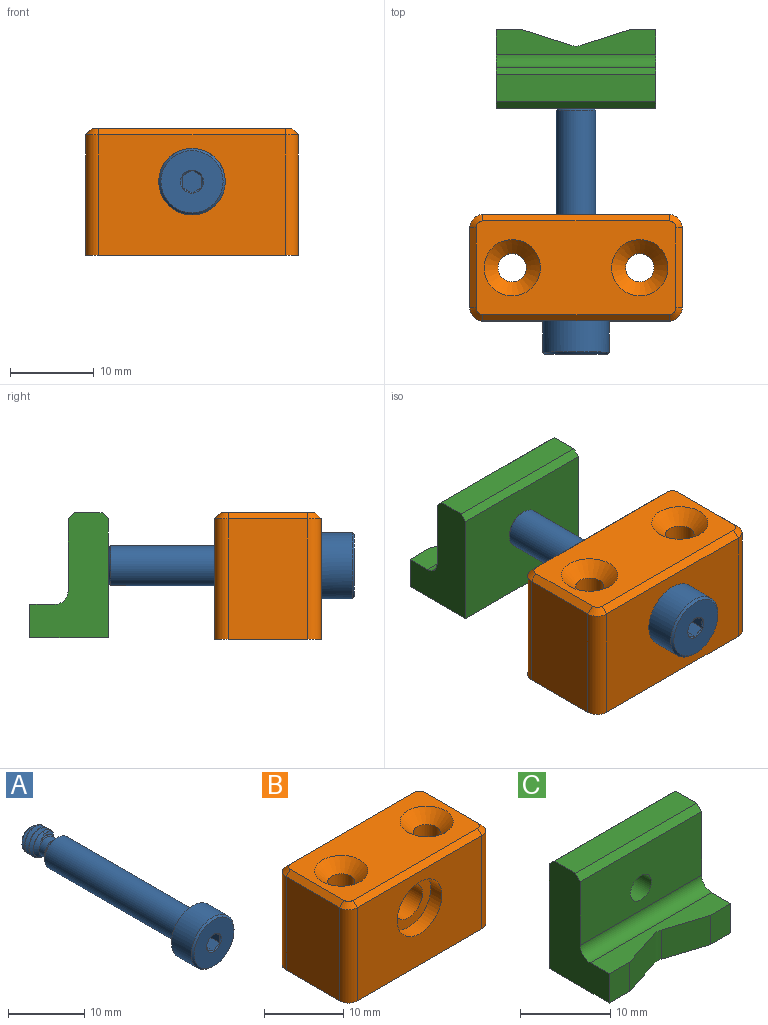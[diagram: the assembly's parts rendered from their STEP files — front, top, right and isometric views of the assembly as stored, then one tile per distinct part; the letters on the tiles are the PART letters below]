
ASSEMBLY  parts=3 mates=1
PART A: 31 faces, bbox 8.5x35x8.5 mm
  f0: cone r=1.42mm half-angle=45deg, axis (0,1,0), area 5.5mm2, adj f1,f6,f7,f8,f9
  f1: bspline ~4.17x4.17mm, area 20mm2, adj f0,f2,f4,f5,f6,f8
  f2: cone r=1.56mm half-angle=45deg, axis (0,-1,0), area 3.7mm2, adj f1,f3,f4,f7,f8
  f3: plane 3.12x3.12mm, normal (0,1,0), area 7.7mm2, adj f2
  f4: cone r=1.56mm half-angle=45deg, axis (0,-1,0), area 0.4mm2, adj f1,f2,f5,f7
  f5: cylinder r=2.08mm len=4.17mm, axis (0,1,0), area 3mm2, adj f1,f4,f6,f7
  f6: cone r=1.42mm half-angle=45deg, axis (0,1,0), area 0.4mm2, adj f0,f1,f5,f7
  f7: bspline ~4.17x4.17mm, area 20mm2, adj f0,f2,f4,f5,f6,f8
  f8: cylinder r=1.57mm len=3.13mm, axis (0,1,0), area 3.5mm2, adj f0,f1,f2,f7
  f9: cylinder r=1.42mm len=2.85mm, axis (0,1,0), area 9.8mm2, adj f0,f10
  f10: torus R=2.08mm, axis (0,1,0), area 10.8mm2, adj f9,f11
  f11: plane 4.25x4.25mm, normal (0,1,0), area 0.5mm2, adj f10,f12
  f12: cone r=2.12mm half-angle=45deg, axis (0,-1,0), area 5.2mm2, adj f11,f13
  f13: cylinder r=2.38mm len=25.14mm, axis (0,1,0), area 376.2mm2, adj f12,f14
  f14: plane 7.94x7.94mm, normal (0,1,0), area 31.7mm2, adj f13,f15
  f15: cylinder r=3.97mm len=7.94mm, axis (0,1,0), area 92.5mm2, adj f14,f16
  f16: cone r=3.97mm half-angle=45deg, axis (0,1,0), area 8.8mm2, adj f15,f17
  f17: plane 7.58x7.58mm, normal (0,-1,0), area 37.3mm2, adj f16,f18,f26,f27,f28,f29,f30
  f18: cone r=1.37mm half-angle=45deg, axis (0,-1,0), area 0mm2, adj f17,f19
  f19: plane 2.51x1.9mm, normal (-1,0,0), area 2.6mm2, adj f18,f20,f24,f25
  f20: plane 2.75x2.38mm, normal (0,-1,0), area 4.9mm2, adj f19,f21,f22,f23,f24,f25
  f21: plane 2.51x1.71mm, normal (0.5,0,0.87), area 2.6mm2, adj f20,f22,f25,f29
  f22: plane 2.51x1.9mm, normal (1,0,0), area 2.6mm2, adj f20,f21,f23,f28
  f23: plane 2.51x1.71mm, normal (0.5,0,-0.87), area 2.6mm2, adj f20,f22,f24,f27
  f24: plane 2.51x1.71mm, normal (-0.5,0,-0.87), area 2.6mm2, adj f19,f20,f23,f26
  f25: plane 2.51x1.71mm, normal (-0.5,0,0.87), area 2.6mm2, adj f19,f20,f21,f30
  f26: cone r=1.37mm half-angle=45deg, axis (0,-1,0), area 0mm2, adj f17,f24
  f27: cone r=1.37mm half-angle=45deg, axis (0,-1,0), area 0mm2, adj f17,f23
  f28: cone r=1.37mm half-angle=45deg, axis (0,-1,0), area 0mm2, adj f17,f22
  f29: cone r=1.37mm half-angle=45deg, axis (0,-1,0), area 0mm2, adj f17,f21
  f30: cone r=1.37mm half-angle=45deg, axis (0,-1,0), area 0mm2, adj f17,f25
PART B: 25 faces, bbox 25.4x12.7x15.2 mm
  f0: cylinder r=4mm len=8mm, axis (0,1,0), area 50.3mm2, adj f4,f24
  f1: plane 14.4x9.53mm, normal (1,0,0), area 137.2mm2, adj f10,f13,f14,f18
  f2: plane 22.23x14.4mm, normal (0,1,0), area 300.2mm2, adj f10,f11,f13,f22,f23
  f3: plane 14.4x9.53mm, normal (-1,0,0), area 137.2mm2, adj f10,f11,f12,f19
  f4: plane 22.23x14.4mm, normal (0,-1,0), area 269.8mm2, adj f0,f10,f12,f14,f15
  f5: cylinder r=1.7mm len=13.5mm, axis (0,0,1), area 144.2mm2, adj f8,f10
  f6: cylinder r=1.7mm len=13.5mm, axis (0,0,1), area 144.2mm2, adj f9,f10
  f7: plane 23.88x11.18mm, normal (0,0,1), area 195.3mm2, adj f8,f9,f15,f16,f17,f18,f19,f20
  f8: cone r=3.36mm half-angle=45deg, axis (0,0,1), area 37.3mm2, adj f5,f7
  f9: cone r=3.36mm half-angle=45deg, axis (0,0,1), area 37.3mm2, adj f6,f7
  f10: plane 25.4x12.7mm, normal (0,0,-1), area 302.3mm2, adj f1,f2,f3,f4,f5,f6,f11,f12
  f11: cylinder r=1.59mm len=14.4mm, axis (0,0,-1), area 35.9mm2, adj f2,f3,f10,f21
  f12: cylinder r=1.59mm len=14.4mm, axis (0,0,-1), area 35.9mm2, adj f3,f4,f10,f17
  f13: cylinder r=1.59mm len=14.4mm, axis (0,0,-1), area 35.9mm2, adj f1,f2,f10,f20
  f14: cylinder r=1.59mm len=14.4mm, axis (0,0,-1), area 35.9mm2, adj f1,f4,f10,f16
  f15: plane 22.23x0.76mm, normal (0,-0.71,0.71), area 24mm2, adj f4,f7,f16,f17
  f16: cone r=0.83mm half-angle=45deg, axis (0,0,-1), area 2mm2, adj f7,f14,f15,f18
  f17: cone r=0.83mm half-angle=45deg, axis (0,0,-1), area 2mm2, adj f7,f12,f15,f19
  f18: plane 9.53x0.76mm, normal (0.71,0,0.71), area 10.3mm2, adj f1,f7,f16,f20
  f19: plane 9.53x0.76mm, normal (-0.71,0,0.71), area 10.3mm2, adj f3,f7,f17,f21
  f20: cone r=0.83mm half-angle=45deg, axis (0,0,-1), area 2mm2, adj f7,f13,f18,f22
  f21: cone r=0.83mm half-angle=45deg, axis (0,0,-1), area 2mm2, adj f7,f11,f19,f22
  f22: plane 22.23x0.76mm, normal (0,0.71,0.71), area 24mm2, adj f2,f7,f20,f21
  f23: cylinder r=2.51mm len=10.7mm, axis (0,-1,0), area 169.1mm2, adj f2,f24
  f24: plane 8x8mm, normal (0,-1,0), area 30.4mm2, adj f0,f23
PART C: 16 faces, bbox 19.1x9.4x15 mm
  f0: plane 3.97x3.18mm, normal (0,-1,0), area 12.6mm2, adj f4,f6,f8,f10
  f1: plane 19.05x8.64mm, normal (0,-1,0), area 156mm2, adj f2,f4,f11,f13,f15
  f2: plane 14.95x9.4mm, normal (1,0,0), area 90.3mm2, adj f1,f3,f5,f6,f7,f10,f12,f13
  f3: plane 19.05x3.3mm, normal (0,0,1), area 62.9mm2, adj f2,f4,f12,f13
  f4: plane 14.95x9.4mm, normal (-1,0,0), area 90.3mm2, adj f0,f1,f3,f5,f6,f10,f12,f13
  f5: plane 19.05x14.19mm, normal (0,1,0), area 261.8mm2, adj f2,f4,f10,f11,f12
  f6: plane 19.05x2.98mm, normal (0,0,1), area 44mm2, adj f0,f2,f4,f7,f8,f9,f14,f15
  f7: plane 3.97x3.18mm, normal (0,-1,0), area 12.6mm2, adj f2,f6,f9,f10
  f8: plane 5.87x3.97mm, normal (0.3,-0.95,0), area 24.4mm2, adj f0,f6,f10,f14
  f9: plane 5.87x3.97mm, normal (-0.3,-0.95,0), area 24.4mm2, adj f6,f7,f10,f14
  f10: plane 19.05x9.4mm, normal (0,0,-1), area 166.1mm2, adj f0,f2,f4,f5,f7,f8,f9,f14
  f11: cylinder r=1.65mm len=4.83mm, axis (0,1,0), area 50mm2, adj f1,f5
  f12: plane 19.05x0.76mm, normal (0,0.71,0.71), area 20.5mm2, adj f2,f3,f4,f5
  f13: plane 19.05x0.76mm, normal (0,-0.71,0.71), area 20.5mm2, adj f1,f2,f3,f4
  f14: cylinder r=1.59mm len=3.97mm, axis (0,0,-1), area 3.9mm2, adj f6,f8,f9,f10
  f15: cylinder r=1.59mm len=19.05mm, axis (1,0,0), area 47.5mm2, adj f1,f2,f4,f6
PLACE A t=(2.56,-8.53,1.37)mm
PLACE B rot(axis=(0,0,1),180deg) t=(2.56,1.78,-8.16)mm
PLACE C rot(axis=(0,0,1),180deg) t=(2.56,20.83,-0.16)mm
MATE pin_slot C.f11 <-> A.f2  axis (0,-1,0) through (2.56,20.83,1.37)mm
